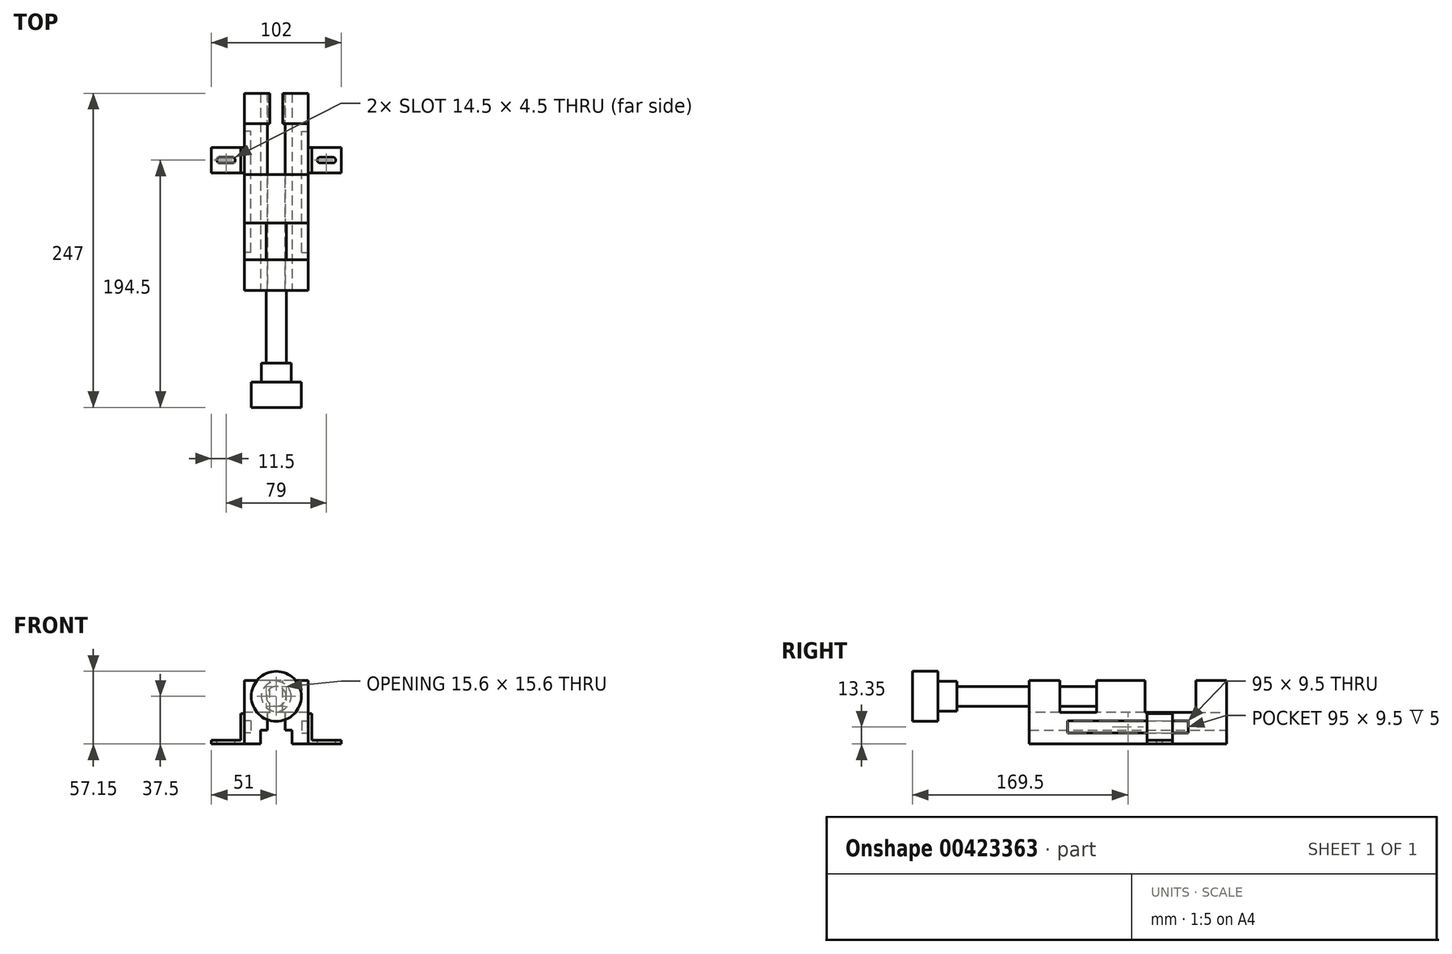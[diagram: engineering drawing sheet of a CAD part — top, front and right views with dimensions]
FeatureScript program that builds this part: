
annotation { "Feature Type Name" : "Feature", "Feature Type Description" : "" }
export const myFeature = defineFeature(function(context is Context, id is Id, definition is map)
    precondition{}
    {
        {
            var Q0;
            Q0=qCreatedBy(makeId("Right.planeOp"),FACE);
            var sketch = newSketch(context, id + "F0", { "sketchPlane" : qUnion([Q0])});
            skLineSegment(sketch, "E0", {"start": v(0, 0) * mm, "end": v(77.5, 0) * mm});
            skLineSegment(sketch, "E1", {"start": v(77.5, 0) * mm, "end": v(77.5, 50) * mm});
            skLineSegment(sketch, "E2", {"start": v(77.5, 50) * mm, "end": v(53.5, 50) * mm});
            skLineSegment(sketch, "E3", {"start": v(53.5, 50) * mm, "end": v(53.5, 25) * mm});
            skLineSegment(sketch, "E4", {"start": v(53.5, 25) * mm, "end": v(0, 25) * mm});
            skLineSegment(sketch, "E5", {"start": v(0, 25) * mm, "end": v(0, 0) * mm});
            skSolve(sketch);
        }
        {
            var Q0;
            Q0 = qSketchRegion(id + "F0", true);
            extrude(context, id + "F1", {"entities" : qUnion([Q0]), "depth" : 25 * mm});
        }
        {
            var Q0;
            Q0=makeQuery(id+"F1.opExtrude","SWEPT_BODY",BODY,{"disambiguationData":[OSD([sQuery(id+"F0.wireOp",EDGE,"E0"),sQuery(id+"F0.wireOp",EDGE,"E1"),sQuery(id+"F0.wireOp",EDGE,"E2"),sQuery(id+"F0.wireOp",EDGE,"E3"),sQuery(id+"F0.wireOp",EDGE,"E4"),sQuery(id+"F0.wireOp",EDGE,"E5")])]});
            var Q1;
            Q1=qCreatedBy(makeId("Front.planeOp"),FACE);
            mirror(context, id + "F2", {"operationType" : NewBodyOperationType.ADD, "entities" : qUnion([Q0]), "mirrorPlane" : qUnion([Q1])});
        }
        {
            var Q0;
            Q0=qCreatedBy(makeId("Right.planeOp"),FACE);
            var sketch = newSketch(context, id + "F3", { "sketchPlane" : qUnion([Q0])});
            skLineSegment(sketch, "E6.bottom", {"start": v(-24.5, 50) * mm, "end": v(13.5, 50) * mm});
            skLineSegment(sketch, "E6.top", {"start": v(-24.5, 25) * mm, "end": v(13.5, 25) * mm});
            skLineSegment(sketch, "E6.left", {"start": v(-24.5, 50) * mm, "end": v(-24.5, 25) * mm});
            skLineSegment(sketch, "E6.right", {"start": v(13.5, 50) * mm, "end": v(13.5, 25) * mm});
            skSolve(sketch);
        }
        {
            var Q0;
            Q0 = qSketchRegion(id + "F3", true);
            extrude(context, id + "F4", {"entities" : qUnion([Q0]), "operationType" : NewBodyOperationType.ADD, "depth" : 25 * mm, "hasSecondDirection" : true, "secondDirectionOppositeDirection" : true, "secondDirectionDepth" : 25 * mm});
        }
        {
            var Q0;
            Q0=makeQuery(id+"F4.opExtrude","SWEPT_FACE",FACE,{"disambiguationData":[OSD([sQuery(id+"F3.wireOp",EDGE,"E6.left")])]});
            var sketch = newSketch(context, id + "F5", { "sketchPlane" : qUnion([Q0])});
            skCircle(sketch, "E7", {"center": v(0, 37.5) * mm, "radius": 7.8 * mm});
            skSolve(sketch);
        }
        {
            var Q0;
            Q0 = qSketchRegion(id + "F5", true);
            extrude(context, id + "F6", {"entities" : qUnion([Q0]), "operationType" : NewBodyOperationType.ADD, "depth" : 110 * mm});
        }
        {
            var Q0;
            Q0=makeQuery(id+"F6.opExtrude","CAP_FACE",FACE,{"disambiguationData":[OSD([sQuery(id+"F5.wireOp",EDGE,"E7")])],"isStart":false});
            var sketch = newSketch(context, id + "F7", { "sketchPlane" : qUnion([Q0])});
            skCircle(sketch, "E8", {"center": v(0, 37.5) * mm, "radius": 11.75 * mm});
            skSolve(sketch);
        }
        {
            var Q0;
            Q0 = qSketchRegion(id + "F7", true);
            extrude(context, id + "F8", {"entities" : qUnion([Q0]), "operationType" : NewBodyOperationType.ADD, "depth" : 15 * mm});
        }
        {
            var Q0;
            Q0=makeQuery(id+"F8.opExtrude","CAP_FACE",FACE,{"disambiguationData":[OSD([sQuery(id+"F7.wireOp",EDGE,"E8")])],"isStart":false});
            var sketch = newSketch(context, id + "F9", { "sketchPlane" : qUnion([Q0])});
            skCircle(sketch, "E9", {"center": v(0, 37.5) * mm, "radius": 19.65 * mm});
            skSolve(sketch);
        }
        {
            var Q0;
            Q0 = qSketchRegion(id + "F9", true);
            extrude(context, id + "F10", {"entities" : qUnion([Q0]), "operationType" : NewBodyOperationType.ADD, "depth" : 20 * mm});
        }
        {
            var Q0;
            {var subQ0=makeQuery(id+"F1.opExtrude","CAP_FACE",FACE,{"disambiguationData":[OSD([sQuery(id+"F0.wireOp",EDGE,"E0"),sQuery(id+"F0.wireOp",EDGE,"E1"),sQuery(id+"F0.wireOp",EDGE,"E2"),sQuery(id+"F0.wireOp",EDGE,"E3"),sQuery(id+"F0.wireOp",EDGE,"E4"),sQuery(id+"F0.wireOp",EDGE,"E5")])],"isStart":false});Q0=makeQuery(id+"F4.boolean.opBoolean","MERGE",FACE,{"derivedFrom":[makeQuery(id+"F2.boolean.opBoolean","MERGE",FACE,{"derivedFrom":[subQ0,makeQuery(id+"F2.opPattern","COPY",FACE,{"derivedFrom":subQ0,"instanceName":"1"})]}),makeQuery(id+"F4.opExtrude","CAP_FACE",FACE,{"disambiguationData":[OSD([sQuery(id+"F3.wireOp",EDGE,"E6.bottom"),sQuery(id+"F3.wireOp",EDGE,"E6.top"),sQuery(id+"F3.wireOp",EDGE,"E6.left"),sQuery(id+"F3.wireOp",EDGE,"E6.right")])],"isStart":false})]});}
            var sketch = newSketch(context, id + "F11", { "sketchPlane" : qUnion([Q0])});
            skLineSegment(sketch, "E10.bottom", {"start": v(-47.5, 18.1) * mm, "end": v(47.5, 18.1) * mm});
            skLineSegment(sketch, "E10.top", {"start": v(-47.5, 8.6) * mm, "end": v(47.5, 8.6) * mm});
            skLineSegment(sketch, "E10.left", {"start": v(-47.5, 18.1) * mm, "end": v(-47.5, 8.6) * mm});
            skLineSegment(sketch, "E10.right", {"start": v(47.5, 18.1) * mm, "end": v(47.5, 8.6) * mm});
            skLineSegment(sketch, "E11", {"start": v(0, 0) * mm, "end": v(0, 37.16) * mm, "construction": true});
            skSolve(sketch);
        }
        {
            var Q0;
            Q0 = qSketchRegion(id + "F11", true);
            extrude(context, id + "F12", {"entities" : qUnion([Q0]), "operationType" : NewBodyOperationType.REMOVE, "oppositeDirection" : true, "depth" : 5 * mm});
        }
        {
            var Q0;
            Q0=makeQuery(id+"F1.opExtrude","SWEPT_BODY",BODY,{"disambiguationData":[OSD([sQuery(id+"F0.wireOp",EDGE,"E0"),sQuery(id+"F0.wireOp",EDGE,"E1"),sQuery(id+"F0.wireOp",EDGE,"E2"),sQuery(id+"F0.wireOp",EDGE,"E3"),sQuery(id+"F0.wireOp",EDGE,"E4"),sQuery(id+"F0.wireOp",EDGE,"E5")])]});
            var Q1;
            Q1=qCreatedBy(makeId("Right.planeOp"),FACE);
            mirror(context, id + "F13", {"operationType" : NewBodyOperationType.ADD, "entities" : qUnion([Q0]), "mirrorPlane" : qUnion([Q1])});
        }
        {
            var Q0;
            Q0=qCreatedBy(makeId("Top.planeOp"),FACE);
            var sketch = newSketch(context, id + "F14", { "sketchPlane" : qUnion([Q0])});
            skLineSegment(sketch, "E12.bottom", {"start": v(-7, -85) * mm, "end": v(7, -85) * mm});
            skLineSegment(sketch, "E12.top", {"start": v(-7, 85) * mm, "end": v(7, 85) * mm});
            skLineSegment(sketch, "E12.left", {"start": v(-7, -85) * mm, "end": v(-7, 85) * mm});
            skLineSegment(sketch, "E12.right", {"start": v(7, -85) * mm, "end": v(7, 85) * mm});
            skPoint(sketch, "E12.middle", {"position": v(0, 0) * mm});
            skSolve(sketch);
        }
        {
            var Q0;
            Q0=makeQuery(id+"F14.imprint","IMPRINT",FACE,{"disambiguationData":[TD([[makeQuery(id+"F14.imprint","IMPRINT",EDGE,{"derivedFrom":sQuery(id+"F14.wireOp",EDGE,"E12.bottom")}),1.0]])]});
            var Q1;
            {var subQ0=sQuery(id+"F0.wireOp",EDGE,"E3");var subQ2=sQuery(id+"F0.wireOp",EDGE,"E4");var subQ10=makeQuery(id+"F1.opExtrude","SWEPT_FACE",FACE,{"disambiguationData":[OSD([subQ2])]});var subQ11=makeQuery(id+"F4.boolean.opBoolean","SPLIT",FACE,{"disambiguationData":[TD([makeQuery(id+"F1.opExtrude","SWEPT_FACE",FACE,{"disambiguationData":[OSD([subQ0])]})])],"derivedFrom":makeQuery(id+"F2.boolean.opBoolean","MERGE",FACE,{"derivedFrom":[subQ10,makeQuery(id+"F2.opPattern","COPY",FACE,{"derivedFrom":subQ10,"instanceName":"1"})]})});Q1=makeQuery(id+"F13.boolean.opBoolean","MERGE",FACE,{"derivedFrom":[subQ11,makeQuery(id+"F13.opPattern","COPY",FACE,{"derivedFrom":subQ11,"instanceName":"1"})]});}
            extrude(context, id + "F15", {"entities" : qUnion([Q0]), "operationType" : NewBodyOperationType.REMOVE, "endBound" : BoundingType.UP_TO_SURFACE, "endBoundEntityFace" : qUnion([Q1]), "depth" : 25 * mm});
        }
        {
            var Q0;
            Q0=qCreatedBy(makeId("Top.planeOp"),FACE);
            var sketch = newSketch(context, id + "F16", { "sketchPlane" : qUnion([Q0])});
            skLineSegment(sketch, "E13.bottom", {"start": v(12.5, 85) * mm, "end": v(-12.5, 85) * mm});
            skLineSegment(sketch, "E13.top", {"start": v(12.5, -85) * mm, "end": v(-12.5, -85) * mm});
            skLineSegment(sketch, "E13.left", {"start": v(12.5, 85) * mm, "end": v(12.5, -85) * mm});
            skLineSegment(sketch, "E13.right", {"start": v(-12.5, 85) * mm, "end": v(-12.5, -85) * mm});
            skPoint(sketch, "E13.middle", {"position": v(0, 0) * mm});
            skSolve(sketch);
        }
        {
            var Q0;
            Q0 = qSketchRegion(id + "F16", true);
            extrude(context, id + "F17", {"entities" : qUnion([Q0]), "operationType" : NewBodyOperationType.REMOVE, "depth" : 11 * mm});
        }
        {
            var Q0;
            {var subQ0=makeQuery(id+"F1.opExtrude","SWEPT_FACE",FACE,{"disambiguationData":[OSD([sQuery(id+"F0.wireOp",EDGE,"E2")])]});Q0=makeQuery(id+"F13.boolean.opBoolean","MERGE",FACE,{"derivedFrom":[subQ0,makeQuery(id+"F13.opPattern","COPY",FACE,{"derivedFrom":subQ0,"instanceName":"1"})]});}
            var sketch = newSketch(context, id + "F18", { "sketchPlane" : qUnion([Q0])});
            skLineSegment(sketch, "E14.bottom", {"start": v(5, 77.5) * mm, "end": v(-5, 77.5) * mm});
            skLineSegment(sketch, "E14.top", {"start": v(5, 53.5) * mm, "end": v(-5, 53.5) * mm});
            skLineSegment(sketch, "E14.left", {"start": v(5, 77.5) * mm, "end": v(5, 53.5) * mm});
            skLineSegment(sketch, "E14.right", {"start": v(-5, 77.5) * mm, "end": v(-5, 53.5) * mm});
            skPoint(sketch, "E14.middle", {"position": v(0, 65.5) * mm});
            skSolve(sketch);
        }
        {
            var Q0;
            Q0 = qSketchRegion(id + "F18", true);
            extrude(context, id + "F19", {"entities" : qUnion([Q0]), "operationType" : NewBodyOperationType.REMOVE, "oppositeDirection" : true, "depth" : 26 * mm});
        }
        {
            var Q0;
            Q0=qCreatedBy(makeId("Right.planeOp"),FACE);
            cPlane(context, id + "F20", {"entities" : qUnion([Q0]), "cplaneType" : CPlaneType.OFFSET, "offset" : 25 * mm, "width" : 150 * mm, "height" : 150 * mm});
        }
        {
            var Q0;
            Q0=qCreatedBy(makeId("Front.planeOp"),FACE);
            cPlane(context, id + "F21", {"entities" : qUnion([Q0]), "cplaneType" : CPlaneType.OFFSET, "offset" : 25 * mm, "oppositeDirection" : true, "width" : 150 * mm, "height" : 150 * mm});
        }
        {
            var Q0;
            Q0=qCreatedBy(id+"F21.planeOp",FACE);
            var sketch = newSketch(context, id + "F22", { "sketchPlane" : qUnion([Q0])});
            skLineSegment(sketch, "E15", {"start": v(51, 0) * mm, "end": v(25, 0) * mm});
            skLineSegment(sketch, "E16", {"start": v(25, 0) * mm, "end": v(25, 24) * mm});
            skLineSegment(sketch, "E17", {"start": v(25, 24) * mm, "end": v(28, 24) * mm});
            skLineSegment(sketch, "E18", {"start": v(28, 24) * mm, "end": v(28, 3) * mm});
            skLineSegment(sketch, "E19", {"start": v(28, 3) * mm, "end": v(51, 3) * mm});
            skLineSegment(sketch, "E20", {"start": v(51, 3) * mm, "end": v(51, 0) * mm});
            skSolve(sketch);
        }
        {
            var Q0;
            Q0 = qSketchRegion(id + "F22", true);
            extrude(context, id + "F23", {"entities" : qUnion([Q0]), "oppositeDirection" : true, "depth" : 10 * mm, "hasSecondDirection" : true, "secondDirectionOppositeDirection" : false, "secondDirectionDepth" : 10 * mm});
        }
        {
            var Q0;
            Q0=makeQuery(id+"F23.opExtrude","SWEPT_FACE",FACE,{"disambiguationData":[OSD([sQuery(id+"F22.wireOp",EDGE,"E19")])]});
            var sketch = newSketch(context, id + "F24", { "sketchPlane" : qUnion([Q0])});
            skLineSegment(sketch, "E21", {"start": v(34.5, 25) * mm, "end": v(44.5, 25) * mm, "construction": true});
            skArc(sketch, "E22.0.startCap", {"start": v(34.5, 22.75) * mm, "mid": v(32.25, 25) * mm, "end": v(34.5, 27.25) * mm});
            skArc(sketch, "E22.0.endCap", {"start": v(44.5, 27.25) * mm, "mid": v(46.75, 25) * mm, "end": v(44.5, 22.75) * mm});
            skLineSegment(sketch, "E22.0.left", {"start": v(34.5, 27.25) * mm, "end": v(44.5, 27.25) * mm});
            skLineSegment(sketch, "E22.0.right", {"start": v(34.5, 22.75) * mm, "end": v(44.5, 22.75) * mm});
            skSolve(sketch);
        }
        {
            var Q0;
            Q0 = qSketchRegion(id + "F24", true);
            extrude(context, id + "F25", {"entities" : qUnion([Q0]), "operationType" : NewBodyOperationType.REMOVE, "endBound" : BoundingType.UP_TO_NEXT, "oppositeDirection" : true, "depth" : 25 * mm});
        }
        {
            var Q0;
            Q0=makeQuery(id+"F23.opExtrude","SWEPT_BODY",BODY,{"disambiguationData":[OSD([sQuery(id+"F22.wireOp",EDGE,"E15"),sQuery(id+"F22.wireOp",EDGE,"E16"),sQuery(id+"F22.wireOp",EDGE,"E17"),sQuery(id+"F22.wireOp",EDGE,"E18"),sQuery(id+"F22.wireOp",EDGE,"E19"),sQuery(id+"F22.wireOp",EDGE,"E20")])]});
            var Q1;
            Q1=qCreatedBy(makeId("Right.planeOp"),FACE);
            mirror(context, id + "F26", {"entities" : qUnion([Q0]), "mirrorPlane" : qUnion([Q1])});
        }
    });
